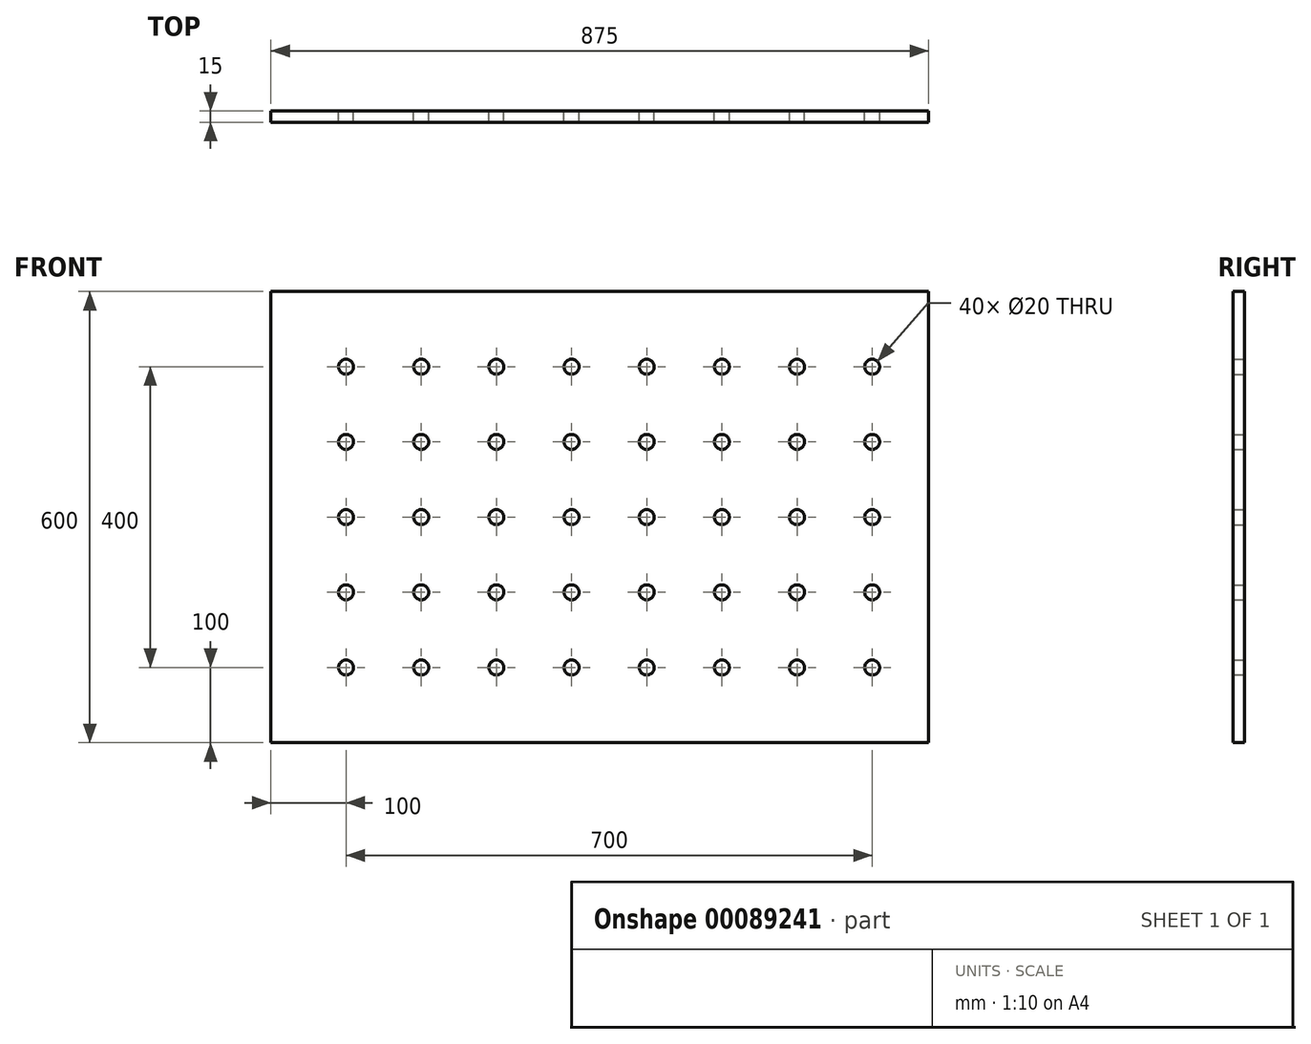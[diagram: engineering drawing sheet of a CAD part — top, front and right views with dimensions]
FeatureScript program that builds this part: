
annotation { "Feature Type Name" : "Feature", "Feature Type Description" : "" }
export const myFeature = defineFeature(function(context is Context, id is Id, definition is map)
    precondition{}
    {
        {
            var Q0;
            Q0=qCreatedBy(makeId("Front.planeOp"),FACE);
            var sketch = newSketch(context, id + "F0", { "sketchPlane" : qUnion([Q0])});
            skLineSegment(sketch, "E0.bottom", {"start": v(-437.5, 300) * mm, "end": v(437.5, 300) * mm});
            skLineSegment(sketch, "E0.top", {"start": v(-437.5, -300) * mm, "end": v(437.5, -300) * mm});
            skLineSegment(sketch, "E0.left", {"start": v(-437.5, 300) * mm, "end": v(-437.5, -300) * mm});
            skLineSegment(sketch, "E0.right", {"start": v(437.5, 300) * mm, "end": v(437.5, -300) * mm});
            skPoint(sketch, "E0.middle", {"position": v(0, 0) * mm});
            skSolve(sketch);
        }
        {
            var Q0;
            Q0=makeQuery(id+"F0.imprint","IMPRINT",FACE,{"disambiguationData":[TD([[makeQuery(id+"F0.imprint","IMPRINT",EDGE,{"derivedFrom":sQuery(id+"F0.wireOp",EDGE,"E0.bottom")}),-1.0]])]});
            extrude(context, id + "F1", {"entities" : qUnion([Q0]), "depth" : 15 * mm});
        }
        {
            var Q0;
            Q0=makeQuery(id+"F1.opExtrude","CAP_FACE",FACE,{"disambiguationData":[OSD([sQuery(id+"F0.wireOp",EDGE,"E0.bottom"),sQuery(id+"F0.wireOp",EDGE,"E0.top"),sQuery(id+"F0.wireOp",EDGE,"E0.left"),sQuery(id+"F0.wireOp",EDGE,"E0.right")])],"isStart":true});
            var sketch = newSketch(context, id + "F2", { "sketchPlane" : qUnion([Q0])});
            skCircle(sketch, "E1", {"center": v(337.5, 200) * mm, "radius": 10 * mm});
            skCircle(sketch, "E2.0.1.0", {"center": v(337.5, 100) * mm, "radius": 10 * mm});
            skCircle(sketch, "E2.0.2.0", {"center": v(337.5, 0) * mm, "radius": 10 * mm});
            skCircle(sketch, "E2.0.3.0", {"center": v(337.5, -100) * mm, "radius": 10 * mm});
            skCircle(sketch, "E2.0.4.0", {"center": v(337.5, -200) * mm, "radius": 10 * mm});
            skCircle(sketch, "E2.1.0.0", {"center": v(237.5, 200) * mm, "radius": 10 * mm});
            skCircle(sketch, "E2.1.1.0", {"center": v(237.5, 100) * mm, "radius": 10 * mm});
            skCircle(sketch, "E2.1.2.0", {"center": v(237.5, 0) * mm, "radius": 10 * mm});
            skCircle(sketch, "E2.1.3.0", {"center": v(237.5, -100) * mm, "radius": 10 * mm});
            skCircle(sketch, "E2.1.4.0", {"center": v(237.5, -200) * mm, "radius": 10 * mm});
            skCircle(sketch, "E2.2.0.0", {"center": v(137.5, 200) * mm, "radius": 10 * mm});
            skCircle(sketch, "E2.2.1.0", {"center": v(137.5, 100) * mm, "radius": 10 * mm});
            skCircle(sketch, "E2.2.2.0", {"center": v(137.5, 0) * mm, "radius": 10 * mm});
            skCircle(sketch, "E2.2.3.0", {"center": v(137.5, -100) * mm, "radius": 10 * mm});
            skCircle(sketch, "E2.2.4.0", {"center": v(137.5, -200) * mm, "radius": 10 * mm});
            skCircle(sketch, "E2.3.0.0", {"center": v(37.5, 200) * mm, "radius": 10 * mm});
            skCircle(sketch, "E2.3.1.0", {"center": v(37.5, 100) * mm, "radius": 10 * mm});
            skCircle(sketch, "E2.3.2.0", {"center": v(37.5, 0) * mm, "radius": 10 * mm});
            skCircle(sketch, "E2.3.3.0", {"center": v(37.5, -100) * mm, "radius": 10 * mm});
            skCircle(sketch, "E2.3.4.0", {"center": v(37.5, -200) * mm, "radius": 10 * mm});
            skCircle(sketch, "E2.4.0.0", {"center": v(-62.5, 200) * mm, "radius": 10 * mm});
            skCircle(sketch, "E2.4.1.0", {"center": v(-62.5, 100) * mm, "radius": 10 * mm});
            skCircle(sketch, "E2.4.2.0", {"center": v(-62.5, 0) * mm, "radius": 10 * mm});
            skCircle(sketch, "E2.4.3.0", {"center": v(-62.5, -100) * mm, "radius": 10 * mm});
            skCircle(sketch, "E2.4.4.0", {"center": v(-62.5, -200) * mm, "radius": 10 * mm});
            skCircle(sketch, "E2.5.0.0", {"center": v(-162.5, 200) * mm, "radius": 10 * mm});
            skCircle(sketch, "E2.5.1.0", {"center": v(-162.5, 100) * mm, "radius": 10 * mm});
            skCircle(sketch, "E2.5.2.0", {"center": v(-162.5, 0) * mm, "radius": 10 * mm});
            skCircle(sketch, "E2.5.3.0", {"center": v(-162.5, -100) * mm, "radius": 10 * mm});
            skCircle(sketch, "E2.5.4.0", {"center": v(-162.5, -200) * mm, "radius": 10 * mm});
            skCircle(sketch, "E2.6.0.0", {"center": v(-262.5, 200) * mm, "radius": 10 * mm});
            skCircle(sketch, "E2.6.1.0", {"center": v(-262.5, 100) * mm, "radius": 10 * mm});
            skCircle(sketch, "E2.6.2.0", {"center": v(-262.5, 0) * mm, "radius": 10 * mm});
            skCircle(sketch, "E2.6.3.0", {"center": v(-262.5, -100) * mm, "radius": 10 * mm});
            skCircle(sketch, "E2.6.4.0", {"center": v(-262.5, -200) * mm, "radius": 10 * mm});
            skCircle(sketch, "E2.7.0.0", {"center": v(-362.5, 200) * mm, "radius": 10 * mm});
            skCircle(sketch, "E2.7.1.0", {"center": v(-362.5, 100) * mm, "radius": 10 * mm});
            skCircle(sketch, "E2.7.2.0", {"center": v(-362.5, 0) * mm, "radius": 10 * mm});
            skCircle(sketch, "E2.7.3.0", {"center": v(-362.5, -100) * mm, "radius": 10 * mm});
            skCircle(sketch, "E2.7.4.0", {"center": v(-362.5, -200) * mm, "radius": 10 * mm});
            skLineSegment(sketch, "E2.direction1", {"start": v(337.5, 200) * mm, "end": v(237.5, 200) * mm, "construction": true});
            skLineSegment(sketch, "E2.direction2", {"start": v(337.5, 200) * mm, "end": v(337.5, 100) * mm, "construction": true});
            skSolve(sketch);
        }
        {
            var Q0;
            Q0=makeQuery(id+"F2.imprint","IMPRINT",FACE,{"disambiguationData":[TD([[makeQuery(id+"F2.imprint","IMPRINT",EDGE,{"derivedFrom":sQuery(id+"F2.wireOp",EDGE,"E2.0.4.0")}),1.0]])]});
            var Q1;
            Q1=makeQuery(id+"F2.imprint","IMPRINT",FACE,{"disambiguationData":[TD([[makeQuery(id+"F2.imprint","IMPRINT",EDGE,{"derivedFrom":sQuery(id+"F2.wireOp",EDGE,"E2.0.3.0")}),1.0]])]});
            var Q2;
            Q2=makeQuery(id+"F2.imprint","IMPRINT",FACE,{"disambiguationData":[TD([[makeQuery(id+"F2.imprint","IMPRINT",EDGE,{"derivedFrom":sQuery(id+"F2.wireOp",EDGE,"E2.0.2.0")}),1.0]])]});
            var Q3;
            Q3=makeQuery(id+"F2.imprint","IMPRINT",FACE,{"disambiguationData":[TD([[makeQuery(id+"F2.imprint","IMPRINT",EDGE,{"derivedFrom":sQuery(id+"F2.wireOp",EDGE,"E2.0.1.0")}),1.0]])]});
            var Q4;
            Q4=makeQuery(id+"F2.imprint","IMPRINT",FACE,{"disambiguationData":[TD([[makeQuery(id+"F2.imprint","IMPRINT",EDGE,{"derivedFrom":sQuery(id+"F2.wireOp",EDGE,"E1")}),1.0]])]});
            var Q5;
            Q5=makeQuery(id+"F2.imprint","IMPRINT",FACE,{"disambiguationData":[TD([[makeQuery(id+"F2.imprint","IMPRINT",EDGE,{"derivedFrom":sQuery(id+"F2.wireOp",EDGE,"E2.1.0.0")}),1.0]])]});
            var Q6;
            Q6=makeQuery(id+"F2.imprint","IMPRINT",FACE,{"disambiguationData":[TD([[makeQuery(id+"F2.imprint","IMPRINT",EDGE,{"derivedFrom":sQuery(id+"F2.wireOp",EDGE,"E2.1.1.0")}),1.0]])]});
            var Q7;
            Q7=makeQuery(id+"F2.imprint","IMPRINT",FACE,{"disambiguationData":[TD([[makeQuery(id+"F2.imprint","IMPRINT",EDGE,{"derivedFrom":sQuery(id+"F2.wireOp",EDGE,"E2.1.2.0")}),1.0]])]});
            var Q8;
            Q8=makeQuery(id+"F2.imprint","IMPRINT",FACE,{"disambiguationData":[TD([[makeQuery(id+"F2.imprint","IMPRINT",EDGE,{"derivedFrom":sQuery(id+"F2.wireOp",EDGE,"E2.1.3.0")}),1.0]])]});
            var Q9;
            Q9=makeQuery(id+"F2.imprint","IMPRINT",FACE,{"disambiguationData":[TD([[makeQuery(id+"F2.imprint","IMPRINT",EDGE,{"derivedFrom":sQuery(id+"F2.wireOp",EDGE,"E2.1.4.0")}),1.0]])]});
            var Q10;
            Q10=makeQuery(id+"F2.imprint","IMPRINT",FACE,{"disambiguationData":[TD([[makeQuery(id+"F2.imprint","IMPRINT",EDGE,{"derivedFrom":sQuery(id+"F2.wireOp",EDGE,"E2.2.4.0")}),1.0]])]});
            var Q11;
            Q11=makeQuery(id+"F2.imprint","IMPRINT",FACE,{"disambiguationData":[TD([[makeQuery(id+"F2.imprint","IMPRINT",EDGE,{"derivedFrom":sQuery(id+"F2.wireOp",EDGE,"E2.2.3.0")}),1.0]])]});
            var Q12;
            Q12=makeQuery(id+"F2.imprint","IMPRINT",FACE,{"disambiguationData":[TD([[makeQuery(id+"F2.imprint","IMPRINT",EDGE,{"derivedFrom":sQuery(id+"F2.wireOp",EDGE,"E2.2.2.0")}),1.0]])]});
            var Q13;
            Q13=makeQuery(id+"F2.imprint","IMPRINT",FACE,{"disambiguationData":[TD([[makeQuery(id+"F2.imprint","IMPRINT",EDGE,{"derivedFrom":sQuery(id+"F2.wireOp",EDGE,"E2.2.1.0")}),1.0]])]});
            var Q14;
            Q14=makeQuery(id+"F2.imprint","IMPRINT",FACE,{"disambiguationData":[TD([[makeQuery(id+"F2.imprint","IMPRINT",EDGE,{"derivedFrom":sQuery(id+"F2.wireOp",EDGE,"E2.2.0.0")}),1.0]])]});
            var Q15;
            Q15=makeQuery(id+"F2.imprint","IMPRINT",FACE,{"disambiguationData":[TD([[makeQuery(id+"F2.imprint","IMPRINT",EDGE,{"derivedFrom":sQuery(id+"F2.wireOp",EDGE,"E2.3.0.0")}),1.0]])]});
            var Q16;
            Q16=makeQuery(id+"F2.imprint","IMPRINT",FACE,{"disambiguationData":[TD([[makeQuery(id+"F2.imprint","IMPRINT",EDGE,{"derivedFrom":sQuery(id+"F2.wireOp",EDGE,"E2.4.0.0")}),1.0]])]});
            var Q17;
            Q17=makeQuery(id+"F2.imprint","IMPRINT",FACE,{"disambiguationData":[TD([[makeQuery(id+"F2.imprint","IMPRINT",EDGE,{"derivedFrom":sQuery(id+"F2.wireOp",EDGE,"E2.5.0.0")}),1.0]])]});
            var Q18;
            Q18=makeQuery(id+"F2.imprint","IMPRINT",FACE,{"disambiguationData":[TD([[makeQuery(id+"F2.imprint","IMPRINT",EDGE,{"derivedFrom":sQuery(id+"F2.wireOp",EDGE,"E2.6.0.0")}),1.0]])]});
            var Q19;
            Q19=makeQuery(id+"F2.imprint","IMPRINT",FACE,{"disambiguationData":[TD([[makeQuery(id+"F2.imprint","IMPRINT",EDGE,{"derivedFrom":sQuery(id+"F2.wireOp",EDGE,"E2.4.1.0")}),1.0]])]});
            var Q20;
            Q20=makeQuery(id+"F2.imprint","IMPRINT",FACE,{"disambiguationData":[TD([[makeQuery(id+"F2.imprint","IMPRINT",EDGE,{"derivedFrom":sQuery(id+"F2.wireOp",EDGE,"E2.3.1.0")}),1.0]])]});
            var Q21;
            Q21=makeQuery(id+"F2.imprint","IMPRINT",FACE,{"disambiguationData":[TD([[makeQuery(id+"F2.imprint","IMPRINT",EDGE,{"derivedFrom":sQuery(id+"F2.wireOp",EDGE,"E2.3.2.0")}),1.0]])]});
            var Q22;
            Q22=makeQuery(id+"F2.imprint","IMPRINT",FACE,{"disambiguationData":[TD([[makeQuery(id+"F2.imprint","IMPRINT",EDGE,{"derivedFrom":sQuery(id+"F2.wireOp",EDGE,"E2.3.3.0")}),1.0]])]});
            var Q23;
            Q23=makeQuery(id+"F2.imprint","IMPRINT",FACE,{"disambiguationData":[TD([[makeQuery(id+"F2.imprint","IMPRINT",EDGE,{"derivedFrom":sQuery(id+"F2.wireOp",EDGE,"E2.3.4.0")}),1.0]])]});
            var Q24;
            Q24=makeQuery(id+"F2.imprint","IMPRINT",FACE,{"disambiguationData":[TD([[makeQuery(id+"F2.imprint","IMPRINT",EDGE,{"derivedFrom":sQuery(id+"F2.wireOp",EDGE,"E2.4.4.0")}),1.0]])]});
            var Q25;
            Q25=makeQuery(id+"F2.imprint","IMPRINT",FACE,{"disambiguationData":[TD([[makeQuery(id+"F2.imprint","IMPRINT",EDGE,{"derivedFrom":sQuery(id+"F2.wireOp",EDGE,"E2.4.3.0")}),1.0]])]});
            var Q26;
            Q26=makeQuery(id+"F2.imprint","IMPRINT",FACE,{"disambiguationData":[TD([[makeQuery(id+"F2.imprint","IMPRINT",EDGE,{"derivedFrom":sQuery(id+"F2.wireOp",EDGE,"E2.4.2.0")}),1.0]])]});
            var Q27;
            Q27=makeQuery(id+"F2.imprint","IMPRINT",FACE,{"disambiguationData":[TD([[makeQuery(id+"F2.imprint","IMPRINT",EDGE,{"derivedFrom":sQuery(id+"F2.wireOp",EDGE,"E2.5.2.0")}),1.0]])]});
            var Q28;
            Q28=makeQuery(id+"F2.imprint","IMPRINT",FACE,{"disambiguationData":[TD([[makeQuery(id+"F2.imprint","IMPRINT",EDGE,{"derivedFrom":sQuery(id+"F2.wireOp",EDGE,"E2.5.3.0")}),1.0]])]});
            var Q29;
            Q29=makeQuery(id+"F2.imprint","IMPRINT",FACE,{"disambiguationData":[TD([[makeQuery(id+"F2.imprint","IMPRINT",EDGE,{"derivedFrom":sQuery(id+"F2.wireOp",EDGE,"E2.5.4.0")}),1.0]])]});
            var Q30;
            Q30=makeQuery(id+"F2.imprint","IMPRINT",FACE,{"disambiguationData":[TD([[makeQuery(id+"F2.imprint","IMPRINT",EDGE,{"derivedFrom":sQuery(id+"F2.wireOp",EDGE,"E2.6.1.0")}),1.0]])]});
            var Q31;
            Q31=makeQuery(id+"F2.imprint","IMPRINT",FACE,{"disambiguationData":[TD([[makeQuery(id+"F2.imprint","IMPRINT",EDGE,{"derivedFrom":sQuery(id+"F2.wireOp",EDGE,"E2.7.0.0")}),1.0]])]});
            var Q32;
            Q32=makeQuery(id+"F2.imprint","IMPRINT",FACE,{"disambiguationData":[TD([[makeQuery(id+"F2.imprint","IMPRINT",EDGE,{"derivedFrom":sQuery(id+"F2.wireOp",EDGE,"E2.7.1.0")}),1.0]])]});
            var Q33;
            Q33=makeQuery(id+"F2.imprint","IMPRINT",FACE,{"disambiguationData":[TD([[makeQuery(id+"F2.imprint","IMPRINT",EDGE,{"derivedFrom":sQuery(id+"F2.wireOp",EDGE,"E2.5.1.0")}),1.0]])]});
            var Q34;
            Q34=makeQuery(id+"F2.imprint","IMPRINT",FACE,{"disambiguationData":[TD([[makeQuery(id+"F2.imprint","IMPRINT",EDGE,{"derivedFrom":sQuery(id+"F2.wireOp",EDGE,"E2.6.2.0")}),1.0]])]});
            var Q35;
            Q35=makeQuery(id+"F2.imprint","IMPRINT",FACE,{"disambiguationData":[TD([[makeQuery(id+"F2.imprint","IMPRINT",EDGE,{"derivedFrom":sQuery(id+"F2.wireOp",EDGE,"E2.7.2.0")}),1.0]])]});
            var Q36;
            Q36=makeQuery(id+"F2.imprint","IMPRINT",FACE,{"disambiguationData":[TD([[makeQuery(id+"F2.imprint","IMPRINT",EDGE,{"derivedFrom":sQuery(id+"F2.wireOp",EDGE,"E2.6.3.0")}),1.0]])]});
            var Q37;
            Q37=makeQuery(id+"F2.imprint","IMPRINT",FACE,{"disambiguationData":[TD([[makeQuery(id+"F2.imprint","IMPRINT",EDGE,{"derivedFrom":sQuery(id+"F2.wireOp",EDGE,"E2.6.4.0")}),1.0]])]});
            var Q38;
            Q38=makeQuery(id+"F2.imprint","IMPRINT",FACE,{"disambiguationData":[TD([[makeQuery(id+"F2.imprint","IMPRINT",EDGE,{"derivedFrom":sQuery(id+"F2.wireOp",EDGE,"E2.7.4.0")}),1.0]])]});
            var Q39;
            Q39=makeQuery(id+"F2.imprint","IMPRINT",FACE,{"disambiguationData":[TD([[makeQuery(id+"F2.imprint","IMPRINT",EDGE,{"derivedFrom":sQuery(id+"F2.wireOp",EDGE,"E2.7.3.0")}),1.0]])]});
            extrude(context, id + "F3", {"entities" : qUnion([Q0, Q1, Q2, Q3, Q4, Q5, Q6, Q7, Q8, Q9, Q10, Q11, Q12, Q13, Q14, Q15, Q16, Q17, Q18, Q19, Q20, Q21, Q22, Q23, Q24, Q25, Q26, Q27, Q28, Q29, Q30, Q31, Q32, Q33, Q34, Q35, Q36, Q37, Q38, Q39]), "operationType" : NewBodyOperationType.REMOVE, "endBound" : BoundingType.THROUGH_ALL, "oppositeDirection" : true, "depth" : 25 * mm});
        }
    });
